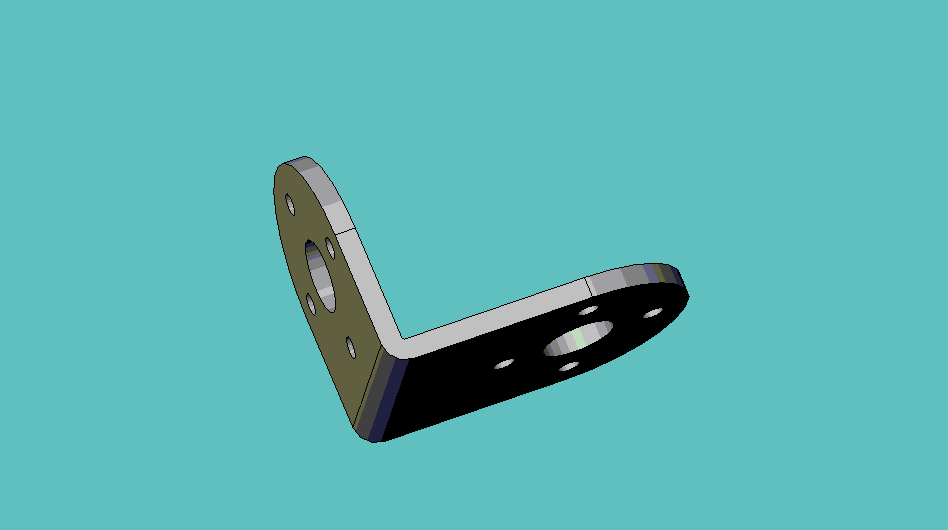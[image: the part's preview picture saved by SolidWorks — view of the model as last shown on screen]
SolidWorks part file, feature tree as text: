
SOLIDWORKS PART (.sldprt)
format: sldprt  version: not decoded by parser v0  size: 199,168 bytes
history: native  units: mm
features: sketch x2, extrude x2, fillet x2, material x1 (+12 scaffold rows collapsed)
feature tree (19):
  scaffold x12  (default folders/planes/origin — collapsed)
  material  "Material <not specified>"
  sketch  "Sketch1"  dims[D1=34.925mm]
  sketch  "Sketch2"  dims[D1=27.6098mm]
  extrude  "Extrude1"  Depth=2.286mm
  extrude  "Extrude2"  Depth=2.286mm
  fillet  "Fillet1"  Radius=0.254mm
  fillet  "Fillet2"  Radius=2.54mm
decode coverage: 6 of 6 modeling features carry decoded parameters
note: suppression state not decoded; provenance and decode notes live in map.json
